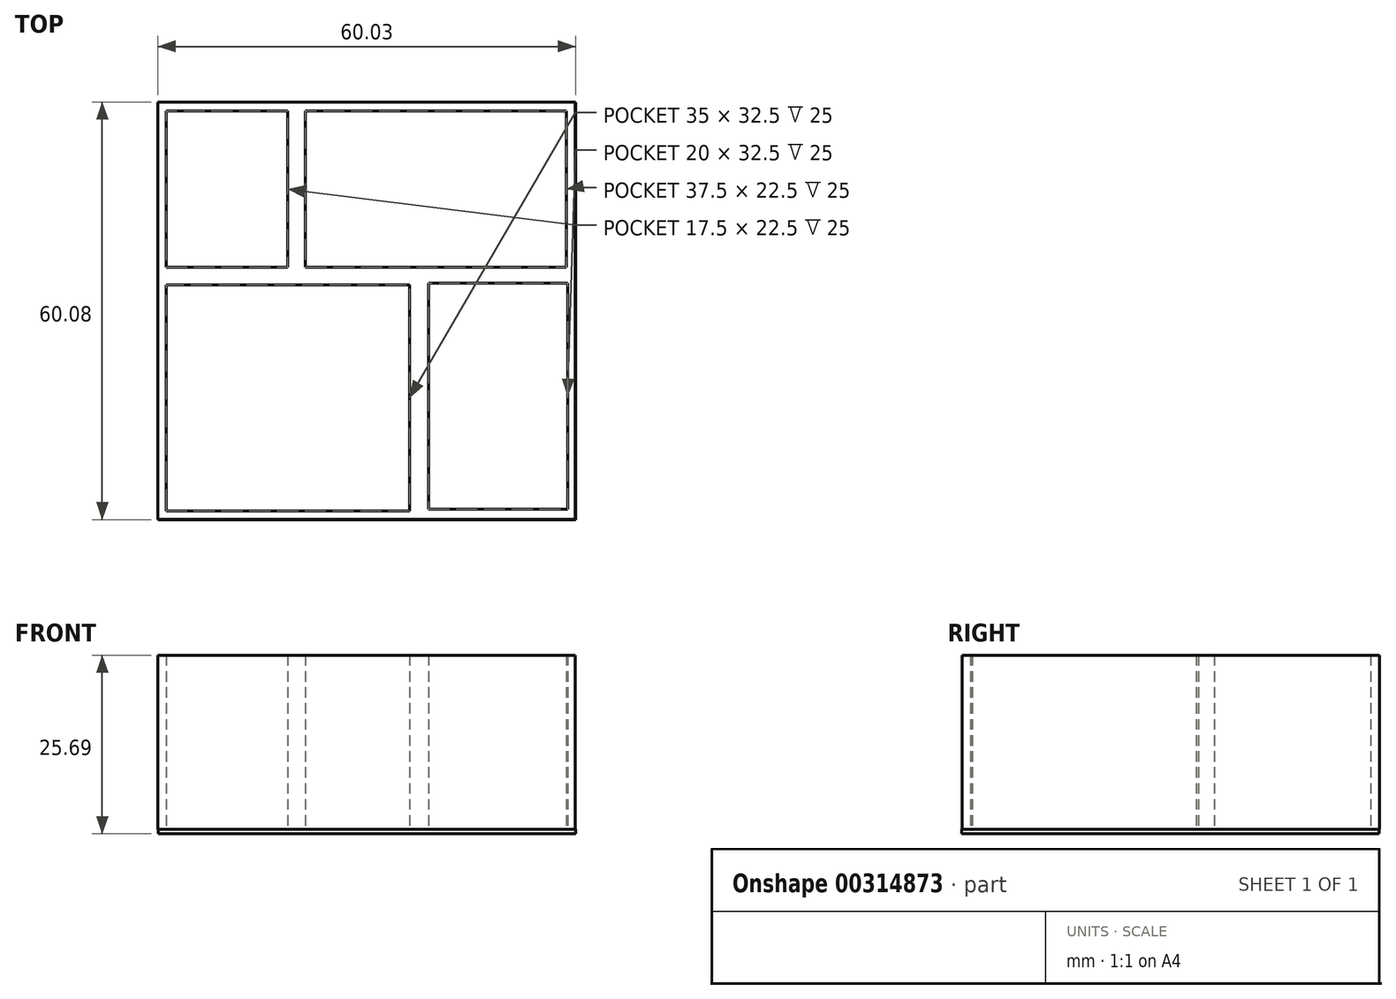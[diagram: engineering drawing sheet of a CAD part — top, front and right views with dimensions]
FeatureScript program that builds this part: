
annotation { "Feature Type Name" : "Feature", "Feature Type Description" : "" }
export const myFeature = defineFeature(function(context is Context, id is Id, definition is map)
    precondition{}
    {
        {
            var Q0;
            Q0=qCreatedBy(makeId("Top.planeOp"),FACE);
            var sketch = newSketch(context, id + "F0", { "sketchPlane" : qUnion([Q0])});
            skLineSegment(sketch, "E0.bottom", {"start": v(-46.3, 39.08) * mm, "end": v(-66.3, 39.08) * mm});
            skLineSegment(sketch, "E0.top", {"start": v(-46.3, 14.08) * mm, "end": v(-66.3, 14.08) * mm});
            skLineSegment(sketch, "E0.left", {"start": v(-46.3, 39.08) * mm, "end": v(-46.3, 14.08) * mm});
            skLineSegment(sketch, "E0.right", {"start": v(-66.3, 39.08) * mm, "end": v(-66.3, 14.08) * mm});
            skLineSegment(sketch, "E1.bottom", {"start": v(-46.3, 14.08) * mm, "end": v(-6.3, 14.08) * mm});
            skLineSegment(sketch, "E1.top", {"start": v(-46.3, 39.08) * mm, "end": v(-6.3, 39.08) * mm});
            skLineSegment(sketch, "E1.left", {"start": v(-46.3, 14.08) * mm, "end": v(-46.3, 39.08) * mm});
            skLineSegment(sketch, "E1.right", {"start": v(-6.3, 14.08) * mm, "end": v(-6.3, 39.08) * mm});
            skLineSegment(sketch, "E2.bottom", {"start": v(-66.3, 14.08) * mm, "end": v(-28.8, 14.08) * mm});
            skLineSegment(sketch, "E2.top", {"start": v(-66.3, -20.92) * mm, "end": v(-28.8, -20.92) * mm});
            skLineSegment(sketch, "E2.left", {"start": v(-66.3, 14.08) * mm, "end": v(-66.3, -20.92) * mm});
            skLineSegment(sketch, "E2.right", {"start": v(-28.8, 14.08) * mm, "end": v(-28.8, -20.92) * mm});
            skLineSegment(sketch, "E3.bottom", {"start": v(-28.8, 14.08) * mm, "end": v(-6.3, 14.08) * mm});
            skLineSegment(sketch, "E3.top", {"start": v(-28.8, -20.92) * mm, "end": v(-6.3, -20.92) * mm});
            skLineSegment(sketch, "E3.right", {"start": v(-6.3, 14.08) * mm, "end": v(-6.3, -20.92) * mm});
            skLineSegment(sketch, "E4.bottom", {"start": v(-65.15, 37.8) * mm, "end": v(-47.65, 37.8) * mm});
            skLineSegment(sketch, "E4.top", {"start": v(-65.15, 15.3) * mm, "end": v(-47.65, 15.3) * mm});
            skLineSegment(sketch, "E4.left", {"start": v(-65.15, 37.8) * mm, "end": v(-65.15, 15.3) * mm});
            skLineSegment(sketch, "E4.right", {"start": v(-47.65, 37.8) * mm, "end": v(-47.65, 15.3) * mm});
            skLineSegment(sketch, "E5.bottom", {"start": v(-45.08, 37.8) * mm, "end": v(-7.58, 37.8) * mm});
            skLineSegment(sketch, "E5.top", {"start": v(-45.08, 15.3) * mm, "end": v(-7.58, 15.3) * mm});
            skLineSegment(sketch, "E5.left", {"start": v(-45.08, 37.8) * mm, "end": v(-45.08, 15.3) * mm});
            skLineSegment(sketch, "E5.right", {"start": v(-7.58, 37.8) * mm, "end": v(-7.58, 15.3) * mm});
            skLineSegment(sketch, "E6.bottom", {"start": v(-65.15, 12.75) * mm, "end": v(-30.15, 12.75) * mm});
            skLineSegment(sketch, "E6.top", {"start": v(-65.15, -19.75) * mm, "end": v(-30.15, -19.75) * mm});
            skLineSegment(sketch, "E6.left", {"start": v(-65.15, 12.75) * mm, "end": v(-65.15, -19.75) * mm});
            skLineSegment(sketch, "E6.right", {"start": v(-30.15, 12.75) * mm, "end": v(-30.15, -19.75) * mm});
            skLineSegment(sketch, "E7.bottom", {"start": v(-27.42, 13.03) * mm, "end": v(-7.42, 13.03) * mm});
            skLineSegment(sketch, "E7.top", {"start": v(-27.42, -19.47) * mm, "end": v(-7.42, -19.47) * mm});
            skLineSegment(sketch, "E7.left", {"start": v(-27.42, 13.03) * mm, "end": v(-27.42, -19.47) * mm});
            skLineSegment(sketch, "E7.right", {"start": v(-7.42, 13.03) * mm, "end": v(-7.42, -19.47) * mm});
            skSolve(sketch);
        }
        {
            var Q0;
            Q0 = qSketchRegion(id + "F0", true);
            extrude(context, id + "F1", {"entities" : qUnion([Q0]), "depth" : 25 * mm});
        }
        {
            var Q0;
            Q0=qCreatedBy(makeId("Front.planeOp"),FACE);
            var sketch = newSketch(context, id + "F2", { "sketchPlane" : qUnion([Q0])});
            skLineSegment(sketch, "E8.bottom", {"start": v(-66.27, 0) * mm, "end": v(-6.27, 0) * mm});
            skLineSegment(sketch, "E8.top", {"start": v(-66.27, -0.7) * mm, "end": v(-6.27, -0.7) * mm});
            skLineSegment(sketch, "E8.left", {"start": v(-66.27, 0) * mm, "end": v(-66.27, -0.7) * mm});
            skLineSegment(sketch, "E8.right", {"start": v(-6.27, 0) * mm, "end": v(-6.27, -0.7) * mm});
            skSolve(sketch);
        }
        {
            var Q0;
            Q0=makeQuery(id+"F2.imprint","IMPRINT",FACE,{"disambiguationData":[TD([[makeQuery(id+"F2.imprint","IMPRINT",EDGE,{"derivedFrom":sQuery(id+"F2.wireOp",EDGE,"E8.bottom")}),-1.0]])]});
            extrude(context, id + "F3", {"entities" : qUnion([Q0]), "operationType" : NewBodyOperationType.ADD, "oppositeDirection" : true, "depth" : 39 * mm});
        }
        {
            var Q0;
            Q0=makeQuery(id+"F3.opExtrude","CAP_FACE",FACE,{"disambiguationData":[OSD([sQuery(id+"F2.wireOp",EDGE,"E8.bottom"),sQuery(id+"F2.wireOp",EDGE,"E8.top"),sQuery(id+"F2.wireOp",EDGE,"E8.left"),sQuery(id+"F2.wireOp",EDGE,"E8.right")])],"isStart":true});
            extrude(context, id + "F4", {"entities" : qUnion([Q0]), "operationType" : NewBodyOperationType.ADD, "depth" : 21 * mm});
        }
    });
